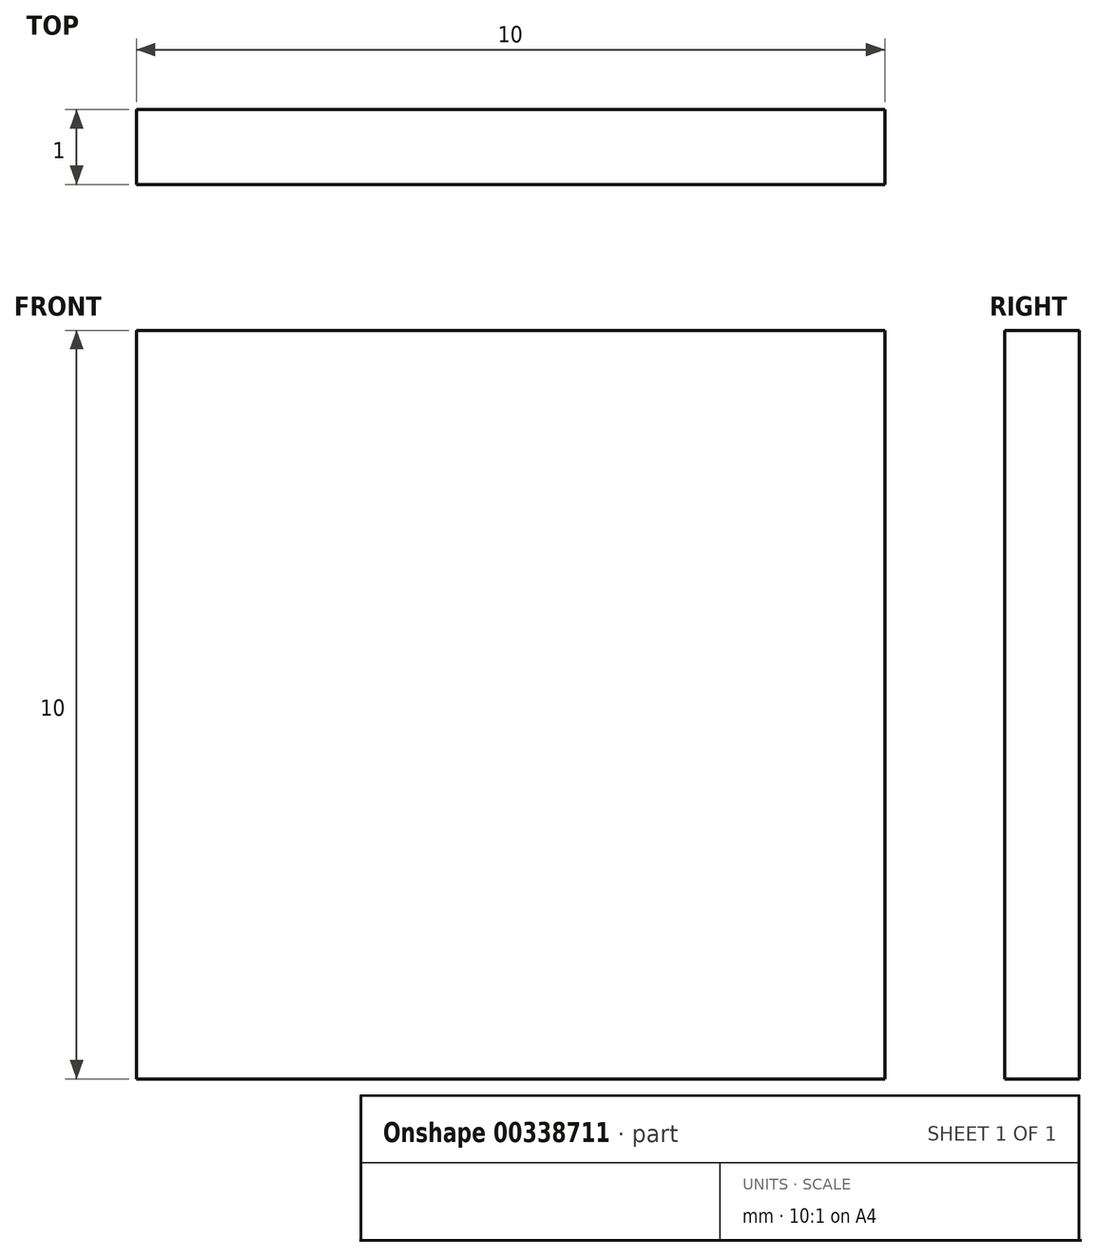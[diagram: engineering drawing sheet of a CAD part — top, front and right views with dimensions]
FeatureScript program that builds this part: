
annotation { "Feature Type Name" : "Feature", "Feature Type Description" : "" }
export const myFeature = defineFeature(function(context is Context, id is Id, definition is map)
    precondition{}
    {
        {
            var Q0;
            Q0=qCreatedBy(makeId("Front.planeOp"),FACE);
            var sketch = newSketch(context, id + "F0", { "sketchPlane" : qUnion([Q0])});
            skLineSegment(sketch, "E0.bottom", {"start": v(5, 5) * mm, "end": v(-5, 5) * mm});
            skLineSegment(sketch, "E0.top", {"start": v(5, -5) * mm, "end": v(-5, -5) * mm});
            skLineSegment(sketch, "E0.left", {"start": v(5, 5) * mm, "end": v(5, -5) * mm});
            skLineSegment(sketch, "E0.right", {"start": v(-5, 5) * mm, "end": v(-5, -5) * mm});
            skPoint(sketch, "E0.middle", {"position": v(0, 0) * mm});
            skLineSegment(sketch, "E1.top", {"start": v(-9, -9) * mm, "end": v(9, -9) * mm});
            skLineSegment(sketch, "E1.left", {"start": v(-9, 9) * mm, "end": v(-9, -9) * mm});
            skLineSegment(sketch, "E1.right", {"start": v(9, 9) * mm, "end": v(9, -9) * mm});
            skPoint(sketch, "E2.middle", {"position": v(-9, -9) * mm});
            skLineSegment(sketch, "E3", {"start": v(5, 9) * mm, "end": v(5, 13) * mm});
            skLineSegment(sketch, "E4", {"start": v(5, 13) * mm, "end": v(9.02, 13) * mm});
            skLineSegment(sketch, "E5", {"start": v(9.02, 13) * mm, "end": v(9, 9) * mm});
            skPoint(sketch, "E6", {"position": v(3, 13) * mm});
            skLineSegment(sketch, "E7", {"start": v(5, 9) * mm, "end": v(-9, 9) * mm});
            skLineSegment(sketch, "E8", {"start": v(9.02, 13) * mm, "end": v(9, -9) * mm});
            skSolve(sketch);
        }
        {
            var Q0;
            Q0=makeQuery(id+"F0.imprint","IMPRINT",FACE,{"disambiguationData":[TD([[makeQuery(id+"F0.imprint","IMPRINT",EDGE,{"derivedFrom":sQuery(id+"F0.wireOp",EDGE,"E0.bottom")}),1.0]])]});
            extrude(context, id + "F1", {"entities" : qUnion([Q0]), "depth" : 0 * mm, "hasSecondDirection" : true, "secondDirectionOppositeDirection" : true, "secondDirectionDepth" : 1 * mm});
        }
    });
